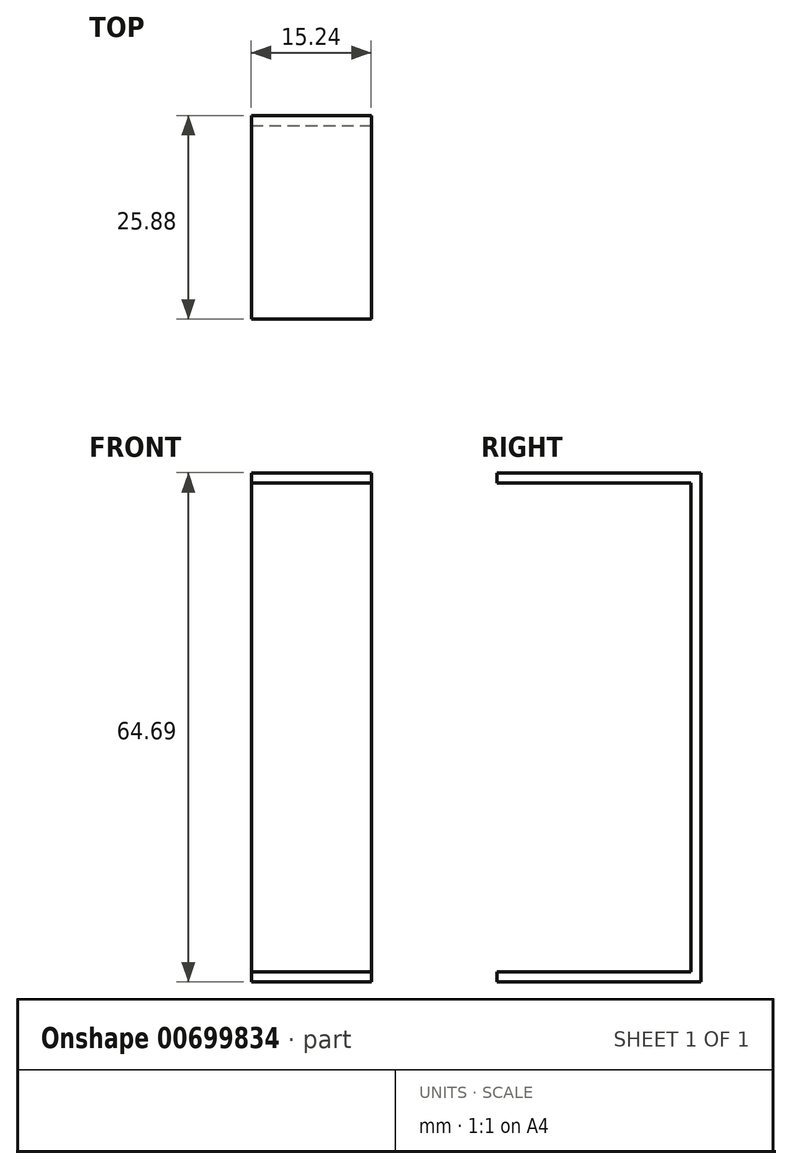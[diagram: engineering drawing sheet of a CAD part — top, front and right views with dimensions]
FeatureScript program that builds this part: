
annotation { "Feature Type Name" : "Feature", "Feature Type Description" : "" }
export const myFeature = defineFeature(function(context is Context, id is Id, definition is map)
    precondition{}
    {
        {
            var Q0;
            Q0=qCreatedBy(makeId("Front.planeOp"),FACE);
            var sketch = newSketch(context, id + "F0", { "sketchPlane" : qUnion([Q0])});
            skLineSegment(sketch, "E0.bottom", {"start": v(-8.17, 31.32) * mm, "end": v(7.07, 31.32) * mm});
            skLineSegment(sketch, "E0.top", {"start": v(-8.17, -33.37) * mm, "end": v(7.07, -33.37) * mm});
            skLineSegment(sketch, "E0.left", {"start": v(-8.17, 31.32) * mm, "end": v(-8.17, -33.37) * mm});
            skLineSegment(sketch, "E0.right", {"start": v(7.07, 31.32) * mm, "end": v(7.07, -33.37) * mm});
            skSolve(sketch);
        }
        {
            var Q0;
            Q0=qSketchRegion(id+"F0",true);
            extrude(context, id + "F1", {"entities" : qUnion([Q0]), "depth" : 1.27 * mm});
        }
        {
            var Q0;
            Q0=makeQuery(id+"F1.opExtrude","SWEPT_FACE",FACE,{"disambiguationData":[OSD([sQuery(id+"F0.wireOp",EDGE,"E0.bottom")])]});
            var sketch = newSketch(context, id + "F2", { "sketchPlane" : qUnion([Q0])});
            skLineSegment(sketch, "E1", {"start": v(7.07, -1.27) * mm, "end": v(7.07, -25.88) * mm});
            skLineSegment(sketch, "E2", {"start": v(-8.17, -1.27) * mm, "end": v(-8.17, -25.88) * mm});
            skLineSegment(sketch, "E3", {"start": v(-8.17, -25.88) * mm, "end": v(7.07, -25.88) * mm});
            skSolve(sketch);
        }
        {
            var Q0;
            Q0=makeQuery(id+"F2.imprint","IMPRINT",FACE,{"disambiguationData":[TD([[makeQuery(id+"F2.imprint","IMPRINT",EDGE,{"derivedFrom":sQuery(id+"F2.wireOp",EDGE,"E1")}),-1.0]])]});
            extrude(context, id + "F3", {"entities" : qUnion([Q0]), "operationType" : NewBodyOperationType.ADD, "depth" : -1.27 * mm});
        }
        {
            var Q0;
            Q0=makeQuery(id+"F1.opExtrude","SWEPT_FACE",FACE,{"disambiguationData":[OSD([sQuery(id+"F0.wireOp",EDGE,"E0.top")])]});
            var sketch = newSketch(context, id + "F4", { "sketchPlane" : qUnion([Q0])});
            skLineSegment(sketch, "E4.bottom", {"start": v(-8.17, 1.27) * mm, "end": v(7.07, 1.27) * mm});
            skLineSegment(sketch, "E4.top", {"start": v(-8.17, 25.88) * mm, "end": v(7.07, 25.88) * mm});
            skLineSegment(sketch, "E4.left", {"start": v(-8.17, 1.27) * mm, "end": v(-8.17, 25.88) * mm});
            skLineSegment(sketch, "E4.right", {"start": v(7.07, 1.27) * mm, "end": v(7.07, 25.88) * mm});
            skSolve(sketch);
        }
        {
            var Q0;
            Q0=makeQuery(id+"F4.imprint","IMPRINT",FACE,{"disambiguationData":[TD([[makeQuery(id+"F4.imprint","IMPRINT",EDGE,{"derivedFrom":sQuery(id+"F4.wireOp",EDGE,"E4.bottom")}),1.0]])]});
            extrude(context, id + "F5", {"entities" : qUnion([Q0]), "operationType" : NewBodyOperationType.ADD, "depth" : -1.27 * mm});
        }
    });
